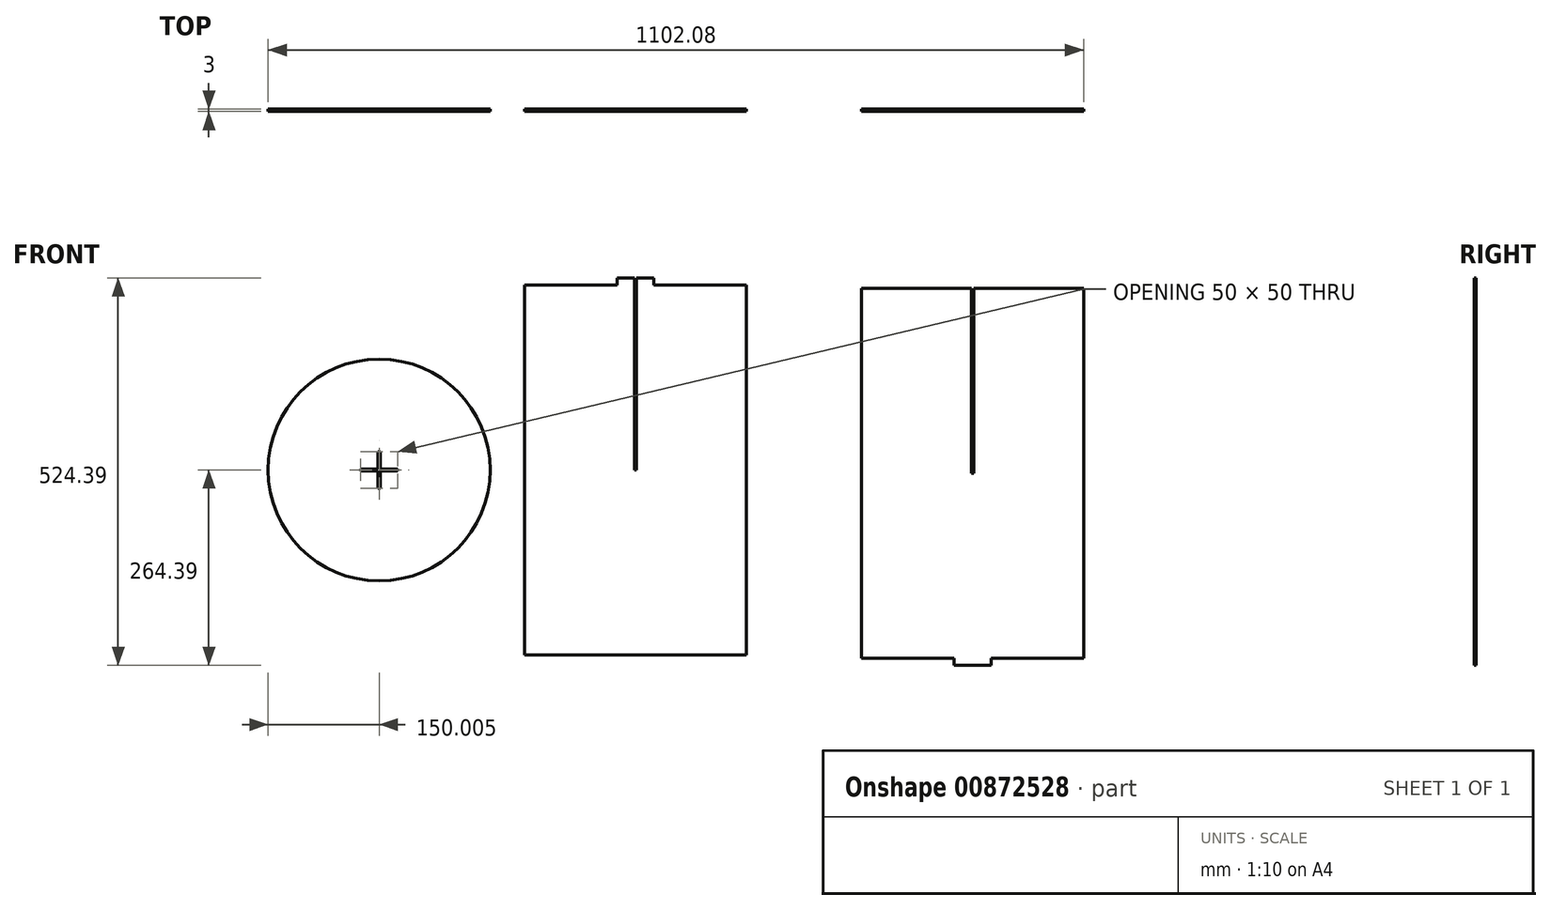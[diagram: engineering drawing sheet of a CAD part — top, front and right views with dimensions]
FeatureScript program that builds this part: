
annotation { "Feature Type Name" : "Feature", "Feature Type Description" : "" }
export const myFeature = defineFeature(function(context is Context, id is Id, definition is map)
    precondition{}
    {
        {
            var Q0;
            Q0=qCreatedBy(makeId("Front.planeOp"),FACE);
            var sketch = newSketch(context, id + "F0", { "sketchPlane" : qUnion([Q0])});
            skLineSegment(sketch, "E0.bottom", {"start": v(-150, -250) * mm, "end": v(150, -250) * mm});
            skLineSegment(sketch, "E0.top", {"start": v(-150, 250) * mm, "end": v(-25, 250) * mm});
            skLineSegment(sketch, "E0.left", {"start": v(-150, -250) * mm, "end": v(-150, 250) * mm});
            skLineSegment(sketch, "E0.right", {"start": v(150, -250) * mm, "end": v(150, 250) * mm});
            skPoint(sketch, "E0.middle", {"position": v(0, 0) * mm});
            skLineSegment(sketch, "E1.left", {"start": v(-1.5, 250) * mm, "end": v(-1.5, 250) * mm});
            skLineSegment(sketch, "E2.bottom", {"start": v(-1.5, 0) * mm, "end": v(1.5, 0) * mm});
            skLineSegment(sketch, "E2.left", {"start": v(-1.5, 0) * mm, "end": v(-1.5, 0) * mm});
            skLineSegment(sketch, "E2.right", {"start": v(1.5, 0) * mm, "end": v(1.5, 0) * mm});
            skLineSegment(sketch, "E3", {"start": v(-1.5, 250) * mm, "end": v(-1.5, 0) * mm});
            skLineSegment(sketch, "E4", {"start": v(1.5, 250) * mm, "end": v(1.5, 0) * mm});
            skLineSegment(sketch, "E5.trimOffspring", {"start": v(25, 250) * mm, "end": v(150, 250) * mm});
            skLineSegment(sketch, "E6.top", {"start": v(25, 260) * mm, "end": v(1.5, 260) * mm});
            skLineSegment(sketch, "E6.left", {"start": v(25, 260) * mm, "end": v(25, 250) * mm});
            skLineSegment(sketch, "E6.right", {"start": v(-25, 260) * mm, "end": v(-25, 250) * mm});
            skPoint(sketch, "E6.middle", {"position": v(0, 255) * mm});
            skPoint(sketch, "E1.right.start.orphan", {"position": v(1.5, 255) * mm});
            skLineSegment(sketch, "E7", {"start": v(-1.5, 250) * mm, "end": v(-1.5, 260) * mm});
            skLineSegment(sketch, "E8", {"start": v(1.5, 250) * mm, "end": v(1.5, 260) * mm});
            skLineSegment(sketch, "E9.trimOffspring", {"start": v(-1.5, 260) * mm, "end": v(-25, 260) * mm});
            skLineSegment(sketch, "E10.bottom", {"start": v(305.75, -254.39) * mm, "end": v(430.75, -254.39) * mm});
            skLineSegment(sketch, "E10.top", {"start": v(305.75, 245.61) * mm, "end": v(430.75, 245.61) * mm});
            skLineSegment(sketch, "E10.left", {"start": v(305.75, -254.39) * mm, "end": v(305.75, 245.61) * mm});
            skLineSegment(sketch, "E10.right", {"start": v(605.75, -254.39) * mm, "end": v(605.75, 245.61) * mm});
            skPoint(sketch, "E10.middle", {"position": v(455.75, -4.39) * mm});
            skLineSegment(sketch, "E11.bottom", {"start": v(454.25, -4.39) * mm, "end": v(457.25, -4.39) * mm});
            skLineSegment(sketch, "E12", {"start": v(454.25, 245.61) * mm, "end": v(454.25, -4.39) * mm});
            skLineSegment(sketch, "E13", {"start": v(457.25, 245.61) * mm, "end": v(457.25, -4.39) * mm});
            skLineSegment(sketch, "E14.trimOffspring", {"start": v(480.75, 245.61) * mm, "end": v(605.75, 245.61) * mm});
            skLineSegment(sketch, "E15.MirrorCS", {"start": v(480.75, -264.39) * mm, "end": v(480.75, -254.39) * mm});
            skLineSegment(sketch, "E16.MirrorCS", {"start": v(480.75, -264.39) * mm, "end": v(457.25, -264.39) * mm});
            skLineSegment(sketch, "E17.MirrorCS", {"start": v(454.25, -264.39) * mm, "end": v(430.75, -264.39) * mm});
            skLineSegment(sketch, "E18.MirrorCS", {"start": v(430.75, -264.39) * mm, "end": v(430.75, -254.39) * mm});
            skLineSegment(sketch, "E19", {"start": v(454.25, -264.39) * mm, "end": v(457.25, -264.39) * mm});
            skLineSegment(sketch, "E20.trimOffspring", {"start": v(480.75, -254.39) * mm, "end": v(605.75, -254.39) * mm});
            skLineSegment(sketch, "E21", {"start": v(430.75, 245.61) * mm, "end": v(454.25, 245.61) * mm});
            skLineSegment(sketch, "E22.trimOffspring", {"start": v(457.25, 245.61) * mm, "end": v(480.75, 245.61) * mm});
            skSolve(sketch);
        }
        {
            var Q0;
            Q0=qSketchRegion(id+"F0",true);
            extrude(context, id + "F1", {"entities" : qUnion([Q0]), "depth" : 3 * mm, "offsetDistance" : 25 * mm});
        }
        {
            var Q0;
            Q0=qCreatedBy(makeId("Front.planeOp"),FACE);
            var sketch = newSketch(context, id + "F2", { "sketchPlane" : qUnion([Q0])});
            skCircle(sketch, "E23", {"center": v(-346.33, 0) * mm, "radius": 150 * mm});
            skLineSegment(sketch, "E24.bottom", {"start": v(-371.33, -1.5) * mm, "end": v(-347.83, -1.5) * mm});
            skLineSegment(sketch, "E24.top", {"start": v(-371.33, 1.5) * mm, "end": v(-347.83, 1.5) * mm});
            skLineSegment(sketch, "E24.left", {"start": v(-371.33, -1.5) * mm, "end": v(-371.33, 1.5) * mm});
            skLineSegment(sketch, "E24.right", {"start": v(-321.33, -1.5) * mm, "end": v(-321.33, 1.5) * mm});
            skLineSegment(sketch, "E25.bottom", {"start": v(-347.83, -25) * mm, "end": v(-344.83, -25) * mm});
            skLineSegment(sketch, "E25.top", {"start": v(-347.83, 25) * mm, "end": v(-344.83, 25) * mm});
            skLineSegment(sketch, "E25.left", {"start": v(-347.83, -25) * mm, "end": v(-347.83, -1.5) * mm});
            skLineSegment(sketch, "E25.right", {"start": v(-344.83, -25) * mm, "end": v(-344.83, -1.5) * mm});
            skLineSegment(sketch, "E26.trimOffspring", {"start": v(-344.83, 1.5) * mm, "end": v(-321.33, 1.5) * mm});
            skLineSegment(sketch, "E27.trimOffspring", {"start": v(-347.83, 1.5) * mm, "end": v(-347.83, 25) * mm});
            skLineSegment(sketch, "E28.trimOffspring", {"start": v(-344.83, -1.5) * mm, "end": v(-321.33, -1.5) * mm});
            skLineSegment(sketch, "E29.trimOffspring", {"start": v(-344.83, 1.5) * mm, "end": v(-344.83, 25) * mm});
            skSolve(sketch);
        }
        {
            var Q0;
            Q0 = qSketchRegion(id + "F2", true);
            extrude(context, id + "F3", {"entities" : qUnion([Q0]), "depth" : 3 * mm, "offsetDistance" : 25 * mm});
        }
    });
